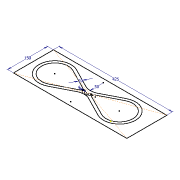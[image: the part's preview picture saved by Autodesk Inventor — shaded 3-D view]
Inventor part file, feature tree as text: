
AUTODESK INVENTOR PART (.ipt)
format: ipt  version: 2017 (Build 210142000, 142)  size: 79,360 bytes
history: native  units: mm
features: sketch x1
ambient origin geometry x8: Origin, YZ Plane, XZ Plane, XY Plane, X Axis, Y Axis, Z Axis, Center Point
feature tree (1):
  sketch  "Sketch1"  dims[d3=10.0mm d4=425.0mm d5=150.0mm d6=50.0mm d7=6.0mm d8=4.0mm]
